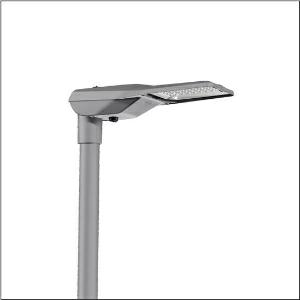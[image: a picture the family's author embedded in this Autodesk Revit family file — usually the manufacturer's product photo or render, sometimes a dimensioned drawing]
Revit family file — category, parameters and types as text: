
# Revit family: streetlight_sl_21_iq_mini___p1_0a_5xe2a31y08gb_f1ed
name_source: partatom
category: Lighting Fixtures
units: mm (PartAtom-declared; Revit-internal decimal feet)

## family parameters
Cut with Voids When Loaded = No
Host = Face
Light Source = No
Part Type = Normal
Room Calculation Point = No
Round Connector Dimension = Use Diameter
Shared = No

## types (1)
- --- (1 x LED, 5990 lm, 39.8 W, 3000K)
    Apparent Load = 40 VA
    CIE Flux Codes = 21 50 90 100 100
    Color Rendering = 70
    Color Temperature = 3000K
    Default Elevation = 1800 mm
    Description = Streetlight SL 21 iQ mini, mast luminaire, primary light control with lens, of PMMA, primary optical cover: cover, of toughened safety glass, transparent, light distribution: P1.0a, light emission: direct distribution, primary light characteristic: asymmetric, installation type: post-top, side-entry, LED, High Power LED, rated luminous flux: 5.990lm, luminous efficacy: 151lm/W, light colour: 730, colour temperature: 3000K, control: presetting dimming logarithmic, Street-Remote, Auto-Match, Temp-Guard, Lumen-Switch, Night-Set, Smart-Wire, Light-Fading, Desk-Remote (wireless, voltage-free reading and setting of iQ features in the workshop via application-optimized NFC function/RFID function), optimised constant luminous flux control (CLO 2.0), mains connection: 220..240V, AC, 50/60Hz, start of lifetime: 40W, end of service life: 41W, reduction: 18W, luminaire housing, of diecast aluminium, powder-coated, Siteco® metallic grey (DB 702S), corrosivity category C5 mid according to DIN EN ISO 12944, please order mast flange separately, inclination adjustable: 0°, 5°, 10°, 15°, sealing non-destructively replaceable, multi-level sealing system, length: 628mm, width: 235mm, height: 110mm, mast flange for spigot size: 42mm (side-entry): 5XC10008XM4, 60/48mm (side-entry/post-top): 5XC10108XM2, 76/60mm (side-entry/post-top): 5XC10108XM1, Smart Interface below and above, protection rating (complete): IP66, insulation class (complete): insulation class II (safety insulation), certification: CE, ENEC, ENEC+, VDE, impact resistance: IK09, permissible operating ambient temperature for outdoor applications: -40..+50°C, standard-compliant lighting for roads and squares, packaging unit: 1 piece

Light Distribution: P1.0a
    Height = 110 mm
    Lamp = 1 x LED
    Lamp Light Flux = 5990 lm
    Lamp Power = 39.8 W
    Lamp count = 1
    Length = 625 mm
    Luminous efficacy = 151 lm/W
    Manufacturer = Siteco
    ModVariant = No
    Model = 5XE2A31Y08GB
    Number of Poles = 1
    OnlyDefault = Yes
    Power Factor = 1
    Product Name = Streetlight SL 21 iQ mini | P1.0a
    Product group = mast luminaire | pylon top
    ProductGroupID = 6100
    Protection Class = Protection class II
    Protection Degree = IP 66
    RLX_Detail_Level = 1
    RLX_Emergency_Light_Flux = 0 lm
    RLX_Emergency_Type = 0
    RLX_Emergency_Type_DB = No
    RlxData = <blob elided: 104093 chars, md5=b20663d8>
    Socket = socket
    Standby Power = 0 W
    System Light Flux = 5990 lm
    System Power = 40 W
    Type Comments = factory setting: luminous flux: 100 % | dim-lin: 254 | 800 mA
    Type Image = l_1003514.jpg
    URL = http://relux.com
    VarID = @adj_043577
    Voltage = 0 V
    Weight = 0.00 kg
    Width = 234 mm

## geometry (parser evidence)
native form markers: Blend x4, Sweep x12
no freeform markers — native parametric forms only
